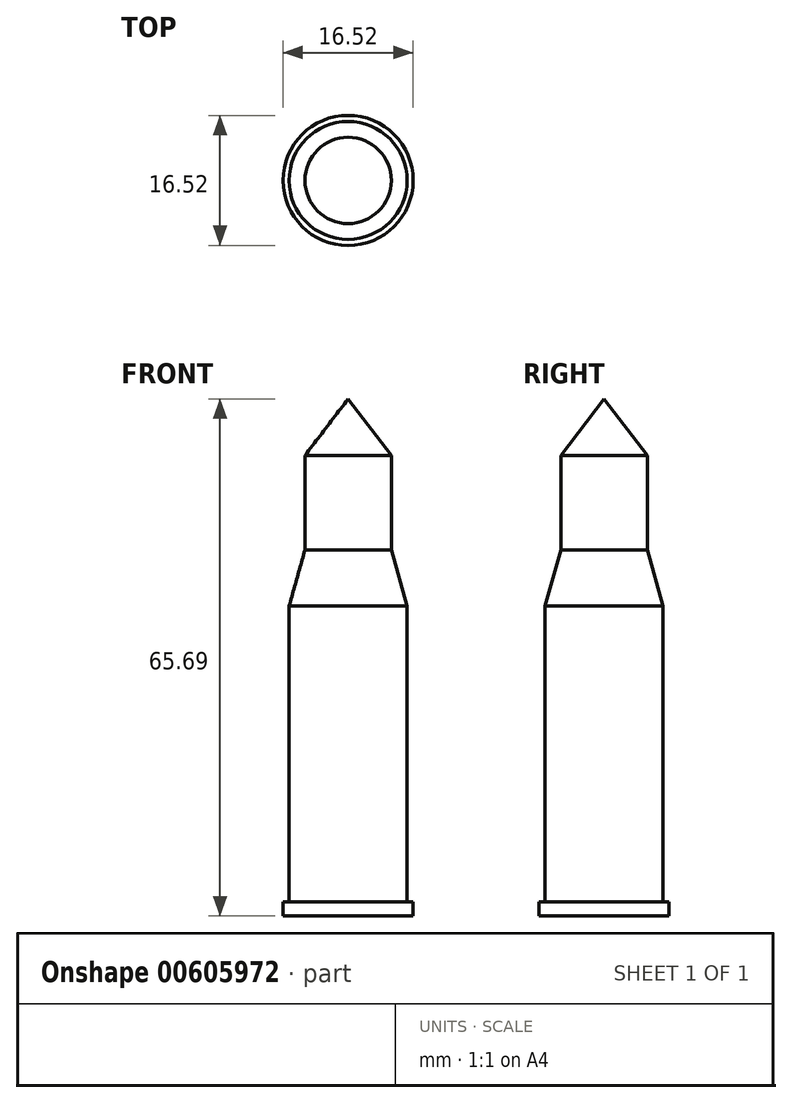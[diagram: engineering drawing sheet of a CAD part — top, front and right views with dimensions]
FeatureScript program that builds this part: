
annotation { "Feature Type Name" : "Feature", "Feature Type Description" : "" }
export const myFeature = defineFeature(function(context is Context, id is Id, definition is map)
    precondition{}
    {
        {
            var Q0;
            Q0=qCreatedBy(makeId("Front.planeOp"),FACE);
            var sketch = newSketch(context, id + "F0", { "sketchPlane" : qUnion([Q0])});
            skLineSegment(sketch, "E0", {"start": v(0, 56.7) * mm, "end": v(-5.48, 49.53) * mm});
            skLineSegment(sketch, "E1", {"start": v(-5.48, 49.53) * mm, "end": v(-5.48, 37.51) * mm});
            skLineSegment(sketch, "E2", {"start": v(-5.48, 37.51) * mm, "end": v(-7.5, 30.4) * mm});
            skLineSegment(sketch, "E3", {"start": v(-7.5, 30.4) * mm, "end": v(-7.5, -7.18) * mm});
            skLineSegment(sketch, "E4", {"start": v(-7.5, -7.18) * mm, "end": v(-8.26, -7.18) * mm});
            skLineSegment(sketch, "E5", {"start": v(-8.26, -7.18) * mm, "end": v(-8.26, -8.98) * mm});
            skLineSegment(sketch, "E6", {"start": v(-8.26, -8.98) * mm, "end": v(0, -8.98) * mm});
            skLineSegment(sketch, "E7", {"start": v(0, -8.98) * mm, "end": v(0, 56.7) * mm});
            skSolve(sketch);
        }
        {
            var Q0;
            Q0 = qSketchRegion(id + "F0", true);
            var Q1;
            Q1=sQuery(id+"F0.wireOp",EDGE,"E7");
            revolve(context, id + "F1", {"entities" : qUnion([Q0]), "axis" : qUnion([Q1]), "revolveType" : RevolveType.FULL});
        }
    });
